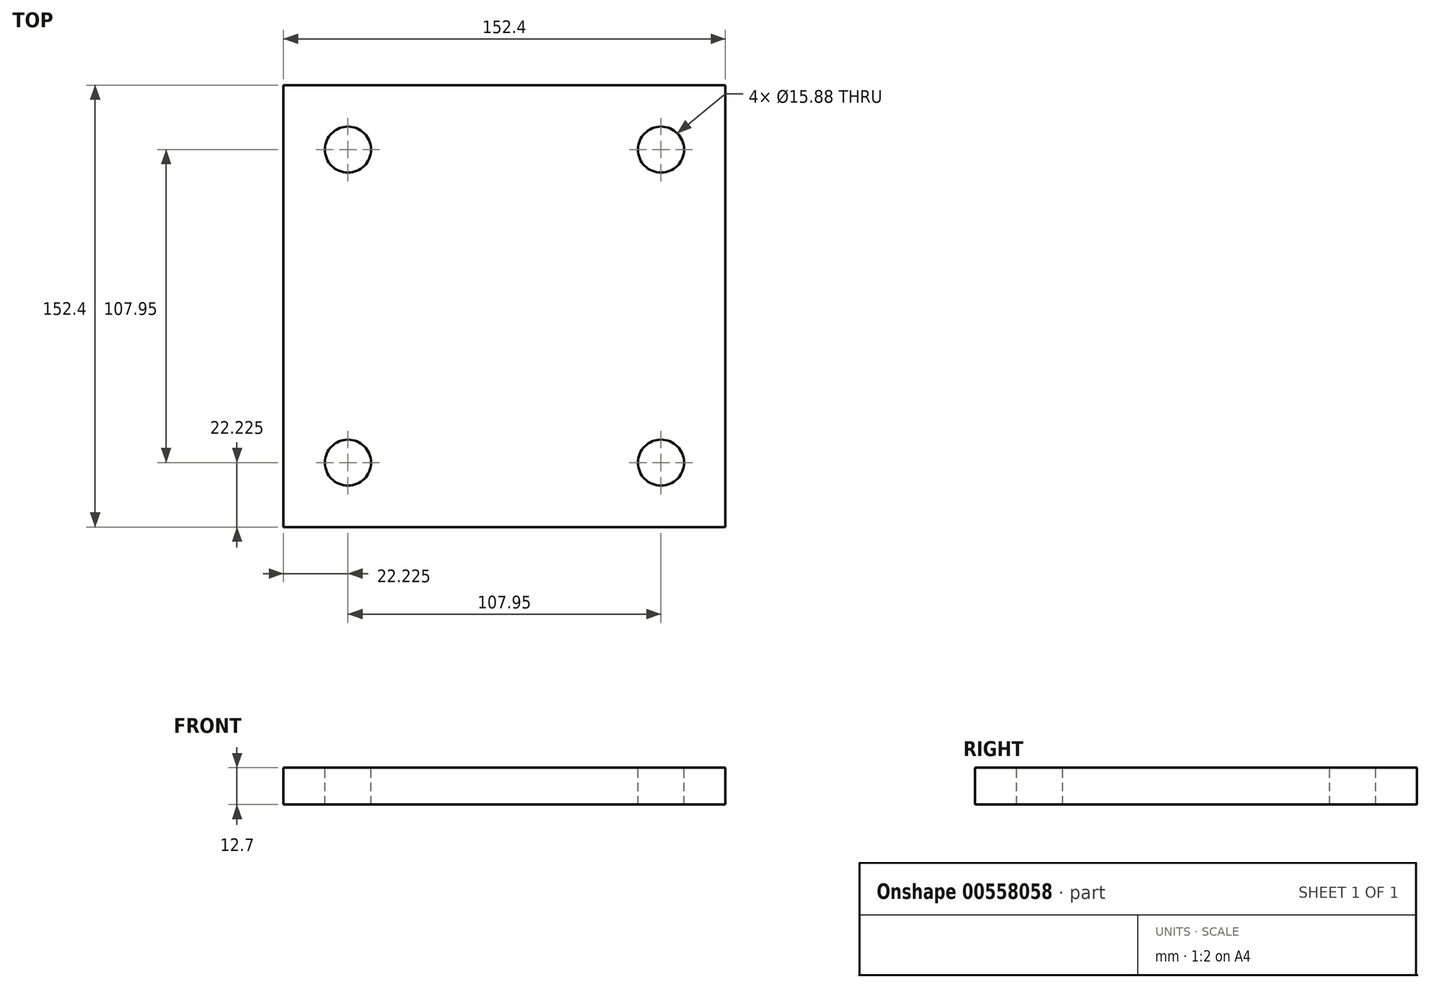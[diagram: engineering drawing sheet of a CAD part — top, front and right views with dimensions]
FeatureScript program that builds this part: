
annotation { "Feature Type Name" : "Feature", "Feature Type Description" : "" }
export const myFeature = defineFeature(function(context is Context, id is Id, definition is map)
    precondition{}
    {
        {
            var Q0;
            Q0=qCreatedBy(makeId("Top.planeOp"),FACE);
            var sketch = newSketch(context, id + "F0", { "sketchPlane" : qUnion([Q0])});
            skLineSegment(sketch, "E0.bottom", {"start": v(76.2, -76.2) * mm, "end": v(-76.2, -76.2) * mm});
            skLineSegment(sketch, "E0.top", {"start": v(76.2, 76.2) * mm, "end": v(-76.2, 76.2) * mm});
            skLineSegment(sketch, "E0.left", {"start": v(76.2, -76.2) * mm, "end": v(76.2, 76.2) * mm});
            skLineSegment(sketch, "E0.right", {"start": v(-76.2, -76.2) * mm, "end": v(-76.2, 76.2) * mm});
            skPoint(sketch, "E0.middle", {"position": v(0, 0) * mm});
            skSolve(sketch);
        }
        {
            var Q0;
            Q0 = qSketchRegion(id + "F0", true);
            extrude(context, id + "F1", {"entities" : qUnion([Q0]), "depth" : 12.7 * mm, "offsetDistance" : 25.4 * mm});
        }
        {
            var Q0;
            Q0=makeQuery(id+"F1.opExtrude","CAP_FACE",FACE,{"disambiguationData":[OSD([sQuery(id+"F0.wireOp",EDGE,"E0.bottom"),sQuery(id+"F0.wireOp",EDGE,"E0.top"),sQuery(id+"F0.wireOp",EDGE,"E0.left"),sQuery(id+"F0.wireOp",EDGE,"E0.right")])],"isStart":false});
            var sketch = newSketch(context, id + "F2", { "sketchPlane" : qUnion([Q0])});
            skCircle(sketch, "E1", {"center": v(-53.98, -53.98) * mm, "radius": 7.94 * mm});
            skCircle(sketch, "E2.MirrorC", {"center": v(53.98, -53.98) * mm, "radius": 7.94 * mm});
            skCircle(sketch, "E3.MirrorC", {"center": v(-53.98, 53.98) * mm, "radius": 7.94 * mm});
            skCircle(sketch, "E4.MirrorC", {"center": v(53.98, 53.98) * mm, "radius": 7.94 * mm});
            skSolve(sketch);
        }
        {
            var Q0;
            Q0 = qSketchRegion(id + "F2", true);
            extrude(context, id + "F3", {"entities" : qUnion([Q0]), "operationType" : NewBodyOperationType.REMOVE, "oppositeDirection" : true, "depth" : 25.4 * mm, "offsetDistance" : 25.4 * mm});
        }
    });
